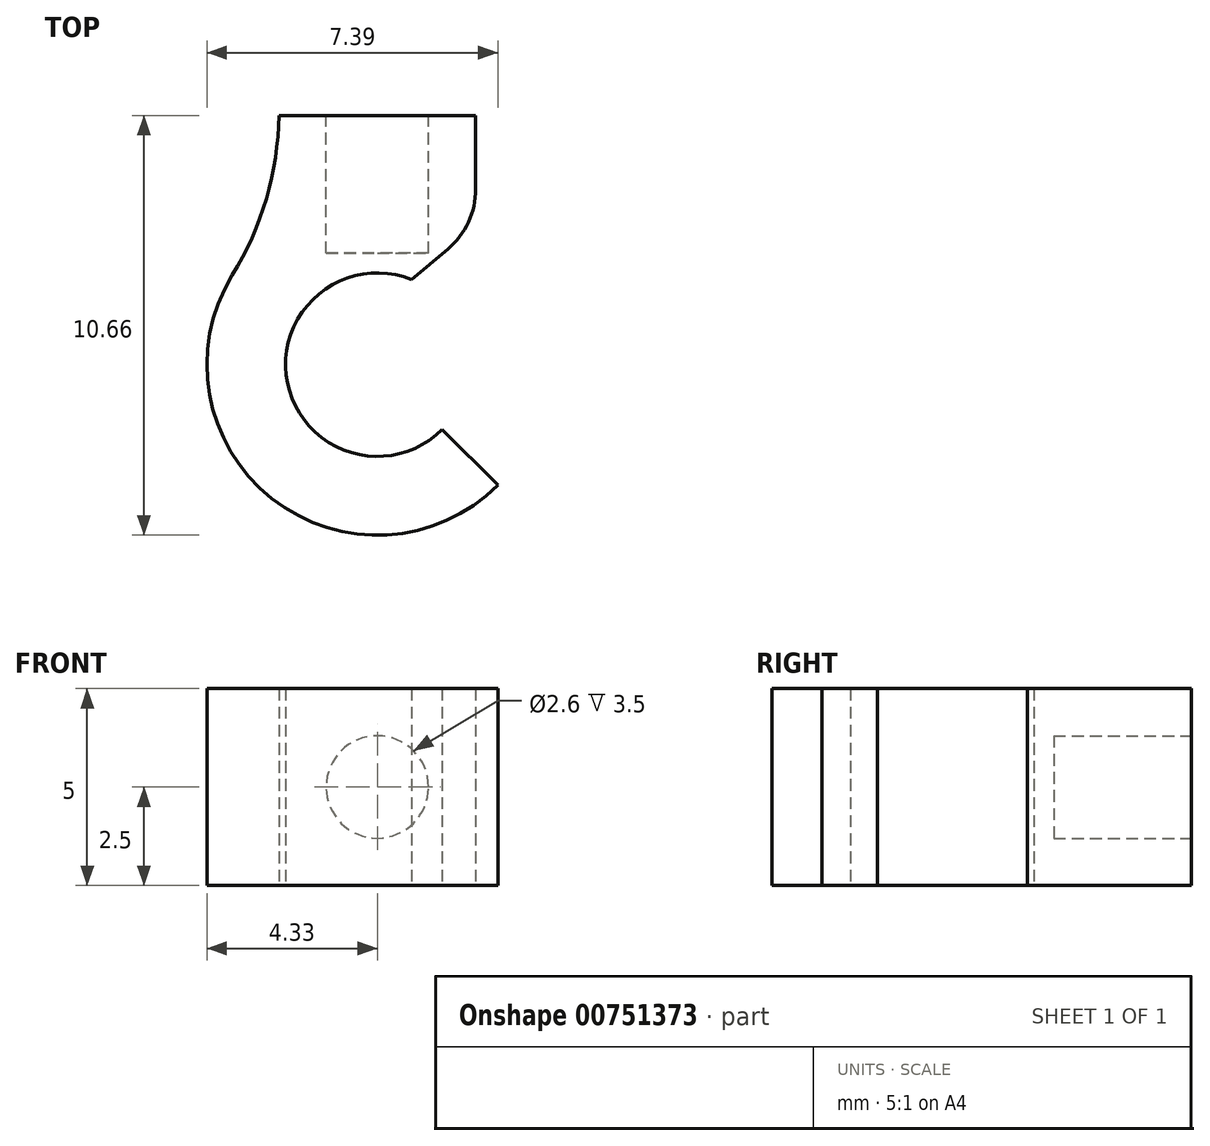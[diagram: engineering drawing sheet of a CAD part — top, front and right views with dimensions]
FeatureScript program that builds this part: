
annotation { "Feature Type Name" : "Feature", "Feature Type Description" : "" }
export const myFeature = defineFeature(function(context is Context, id is Id, definition is map)
    precondition{}
    {
        {
            var Q0;
            Q0=qCreatedBy(makeId("Top.planeOp"),FACE);
            var sketch = newSketch(context, id + "F0", { "sketchPlane" : qUnion([Q0])});
            skArc(sketch, "E0", {"start": v(0.87, 2.16) * mm, "mid": v(-2.28, -0.46) * mm, "end": v(1.65, -1.65) * mm});
            skLineSegment(sketch, "E1", {"start": v(0, 0) * mm, "end": v(0.87, 2.16) * mm, "construction": true});
            skLineSegment(sketch, "E2", {"start": v(0, 0) * mm, "end": v(1.65, -1.65) * mm, "construction": true});
            skArc(sketch, "E3.0", {"start": v(-2.5, 3.54) * mm, "mid": v(-3.31, -2.8) * mm, "end": v(3.06, -3.06) * mm});
            skLineSegment(sketch, "E4", {"start": v(0, 2.33) * mm, "end": v(0, 6.33) * mm, "construction": true});
            skLineSegment(sketch, "E5", {"start": v(-2.5, 6.33) * mm, "end": v(2.5, 6.33) * mm});
            skPoint(sketch, "E6", {"position": v(0, 6.33) * mm});
            skLineSegment(sketch, "E7", {"start": v(-2.5, 6.33) * mm, "end": v(-2.5, 3.54) * mm});
            skLineSegment(sketch, "E8", {"start": v(2.5, 6.33) * mm, "end": v(2.5, 3.54) * mm});
            skLineSegment(sketch, "E9", {"start": v(2.5, 3.54) * mm, "end": v(0.87, 2.16) * mm});
            skLineSegment(sketch, "E10", {"start": v(1.65, -1.65) * mm, "end": v(3.06, -3.06) * mm});
            skSolve(sketch);
        }
        {
            var Q0;
            Q0=makeQuery(id+"F0.imprint","IMPRINT",FACE,{"disambiguationData":[TD([[makeQuery(id+"F0.imprint","IMPRINT",EDGE,{"derivedFrom":sQuery(id+"F0.wireOp",EDGE,"E0")}),-1.0]])]});
            extrude(context, id + "F1", {"entities" : qUnion([Q0]), "depth" : 5 * mm, "offsetDistance" : 25 * mm});
        }
        {
            var Q0;
            Q0=makeQuery(id+"F1.opExtrude","SWEPT_FACE",FACE,{"disambiguationData":[OSD([sQuery(id+"F0.wireOp",EDGE,"E5")])]});
            var sketch = newSketch(context, id + "F2", { "sketchPlane" : qUnion([Q0])});
            skCircle(sketch, "E11", {"center": v(0, 2.5) * mm, "radius": 1.3 * mm});
            skPoint(sketch, "E11.centerSnap0", {"position": v(0, 0) * mm});
            skPoint(sketch, "E11.centerSnap1", {"position": v(2.5, 2.5) * mm});
            skSolve(sketch);
        }
        {
            var Q0;
            Q0=makeQuery(id+"F2.imprint","IMPRINT",FACE,{"disambiguationData":[TD([[makeQuery(id+"F2.imprint","IMPRINT",EDGE,{"derivedFrom":sQuery(id+"F2.wireOp",EDGE,"E11")}),1.0]])]});
            extrude(context, id + "F3", {"entities" : qUnion([Q0]), "operationType" : NewBodyOperationType.REMOVE, "oppositeDirection" : true, "depth" : 3.5 * mm, "offsetDistance" : 25 * mm});
        }
        {
            var Q0;
            Q0=makeQuery(id+"F1.opExtrude","SWEPT_EDGE",EDGE,{"disambiguationData":[OSD([sQuery(id+"F0.wireOp",EDGE,"E3.0"),sQuery(id+"F0.wireOp",EDGE,"E7")])]});
            fillet(context, id + "F4", {"entities" : qUnion([Q0]), "radius" : 8 * mm, "tangentPropagation" : true, "allowEdgeOverflow" : false});
        }
        {
            var Q0;
            Q0=makeQuery(id+"F1.opExtrude","SWEPT_EDGE",EDGE,{"disambiguationData":[OSD([sQuery(id+"F0.wireOp",EDGE,"E8"),sQuery(id+"F0.wireOp",EDGE,"E9")])]});
            fillet(context, id + "F5", {"entities" : qUnion([Q0]), "radius" : 2 * mm, "tangentPropagation" : true, "allowEdgeOverflow" : false});
        }
    });
